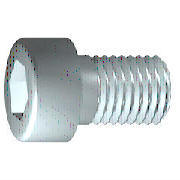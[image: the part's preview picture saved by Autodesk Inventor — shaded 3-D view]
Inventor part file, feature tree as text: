
AUTODESK INVENTOR PART (.ipt)
format: ipt  version: 2020 (Build 240168000, 168)  size: 196,608 bytes
history: native  units: mm (DEFAULTED — no unit token found)
features: sketch x2, extrude x1, plane x1, fillet x1
ambient origin geometry x7: Origin, YZ Plane, XY Plane, X Axis, Y Axis, Z Axis, Center Point
bodies: Solid1 (feature_tree), Body (feature_tree)
feature tree (5):
  extrude  "Slot"  Depth=3.0mm
  plane  "Work Plane1"
  fillet  "Fillet2"  Radius=3.0mm
  sketch  "Sketch1"  dims[d1=4.75mm d2=0.306825mm d3=3.0mm]
  sketch  "Sketch2"  dims[d4=1.3mm d5=60.0deg d6=3.0mm d7=3.0mm d8=2.886751mm d9=5.5mm d10=90.0deg d11=10.0mm d12=0.0mm d13=4.75mm d14=0.0mm d15=0.306725mm d16=0.306725mm d17=0.3mm d19=0.0mm d26=6.0mm d27=45.0deg d28=0.0mm d29=0.0mm d30=0.1mm]
